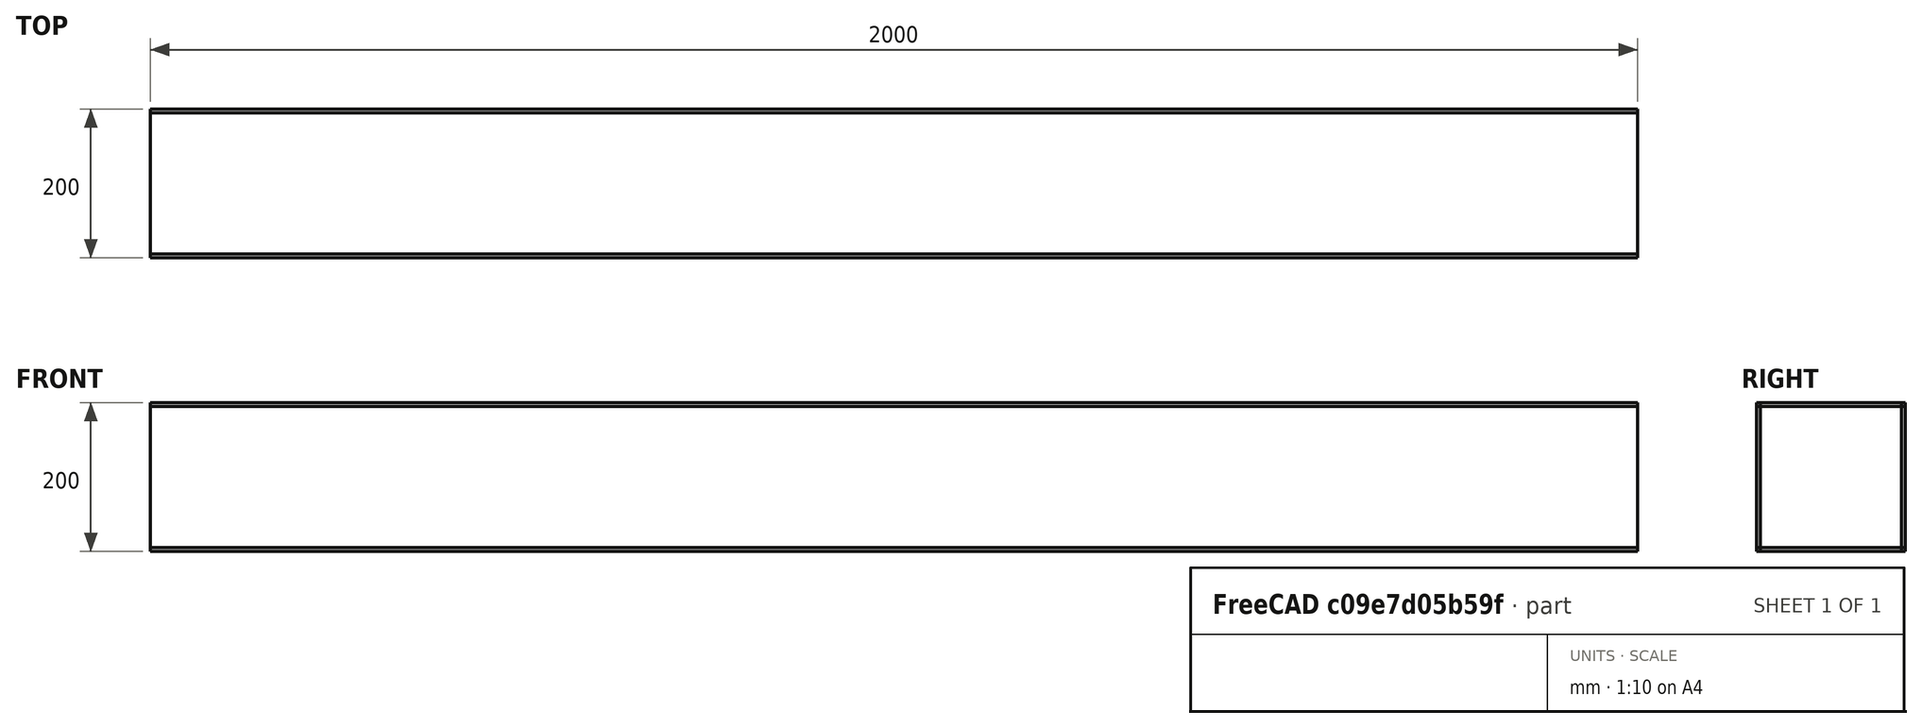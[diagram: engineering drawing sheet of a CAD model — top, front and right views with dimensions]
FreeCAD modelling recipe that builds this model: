
FCSTD DOCUMENT  (FreeCAD 0.21R33771 (Git))
Label: Torsion
License: All rights reserved
LicenseURL: http://en.wikipedia.org/wiki/All_rights_reserved
objects: Part::Box×4, Fem::FemSolverObjectPython×1, App::MaterialObjectPython×1, Part::FeaturePython×1, Fem::ConstraintForce×1, Fem::ConstraintFixed×1, Fem::FemMeshObjectPython×1, Fem::FemAnalysis×1
note: 5 computed .brp shape members not serialized (recipe doc carries the construction recipe); baked Part::Feature solids carry a one-line shape summary decoded from their .brp

FEATURE [Part::Box] Box  label="Cube"
  AttacherType = Attacher::AttachEngine3D
  Height = 200
  Length = 2000
  Width = 5
FEATURE [Fem::FemSolverObjectPython] SolverCcxTools  # FEM object (typed FeaturePython)
  AnalysisType = 0
  BeamReducedIntegration = true
  BeamShellResultOutput3D = true
  BucklingFactors = 1
  EigenmodeHighLimit = 1000000
  EigenmodeLowLimit = 0
  EigenmodesCount = 10
  GeometricalNonlinearity = 0
  IterationsControlParameterCutb = 0.25,0.5,0.75,0.85,,,1.5,
  IterationsControlParameterIter = 4,8,9,200,10,400,,200,,
  IterationsControlParameterTimeUse = false
  IterationsMaximum = 2000
  IterationsThermoMechMaximum = 2000
  IterationsUserDefinedIncrementations = false
  IterationsUserDefinedTimeStepLength = false
  MaterialNonlinearity = 0
  MatrixSolverType = 0
  ModelSpace = 0
  OutputFrequency = 1
  SplitInputWriter = false
  ThermoMechSteadyState = true
  ThermoMechType = 0
  TimeEnd = 1
  TimeInitialStep = 0.01
  TimeMaximumStep = 1
  TimeMinimumStep = 1e-05
FEATURE [App::MaterialObjectPython] MaterialSolid  # material (typed FeaturePython)
  Category = 0
  Material = AmbientColor=(0.0020, 0.0020, 0.0020, 1.0),Author=Juergen Riegel,AuthorAndLicense=CC-BY-3.0,CardName=CalculiX-Steel,Density=7.9e-06 kg/mm^3,+14 more (map truncated)
  UUID = 92589471-a6cb-4bbc-b748-d425a17dea7d
FEATURE [Part::Box] Box001  label="Cube001"
  AttacherType = Attacher::AttachEngine3D
  Height = 200
  Length = 2000
  Placement = pos=(0,195,0) rot=(0,0,1;0rad)
  Width = 5
FEATURE [Part::Box] Box002  label="Cube002"
  AttacherType = Attacher::AttachEngine3D
  Height = 200
  Length = 2000
  Placement = pos=(0,200,195) rot=(1,0,0;1.5708rad)
  Width = 5
FEATURE [Part::Box] Box003  label="Cube003"
  AttacherType = Attacher::AttachEngine3D
  Height = 200
  Length = 2000
  Placement = pos=(0,200,0) rot=(1,0,0;1.5708rad)
  Width = 5
FEATURE [Part::FeaturePython] BooleanFragments  # WARN: FeaturePython — macro-defined, semantics opaque (R4)
  Mode = 2
  Objects = -> [Box,Box001,Box002,Box003]
  Tolerance = 0
FEATURE [Fem::ConstraintForce] ConstraintForce
  Direction = -> Box [Edge6]
  DirectionVector = (0,-1,0)
  Force = 10000
  NormalDirection = (1,0,0)
  Points = (24) [(2000,195,200),(2000,131.667,200),(2000,68.3333,200),(2000,5,200),(2000,195,197.5),(2000,131.667,197.5),(2000,68.3333,197.5),(2000,5,197.5),+16 more]
  References = -> [BooleanFragments]
  Reversed = true
  Scale = 10
FEATURE [Fem::ConstraintFixed] ConstraintFixed
  NormalDirection = (-1,0,0)
  Normals = (84) [(-1,0,0),(-1,0,0),(-1,0,0),(-1,0,0),(-1,0,0),(-1,0,0),(-1,0,0),(-1,0,0),(-1,0,0),(-1,0,0),(-1,0,0),(-1,0,0),(-1,0,0),(-1,0,0),(-1,0,0),(-1,0,0),+68 more]
  Points = (84) [(0,5,195),(0,5,197.5),(0,5,200),(0,2.5,195),(0,2.5,197.5),(0,2.5,200),(0,0,195),(0,0,197.5),(0,0,200),(0,200,195),(0,200,197.5),(0,200,200),+72 more]
  References = -> [BooleanFragments]
  Scale = 10
FEATURE [Fem::FemMeshObjectPython] FEMMeshGmsh  # FEM object (typed FeaturePython)
  Algorithm2D = 0
  Algorithm3D = 0
  CharacteristicLengthMax = 50
  CharacteristicLengthMin = 0
  CoherenceMesh = true
  ElementDimension = 0
  ElementOrder = 1
  GeometryTolerance = 1e-06
  GroupsOfNodes = false
  HighOrderOptimize = 0
  MeshSizeFromCurvature = 12
  OptimizeNetgen = false
  OptimizeStd = true
  Part = -> BooleanFragments
  RecombinationAlgorithm = 0
  Recombine3DAll = false
  RecombineAll = false
  SecondOrderLinear = false
FEATURE [Fem::FemAnalysis] Analysis
  Group = -> [ConstraintForce,ConstraintFixed,SolverCcxTools,MaterialSolid,FEMMeshGmsh]
